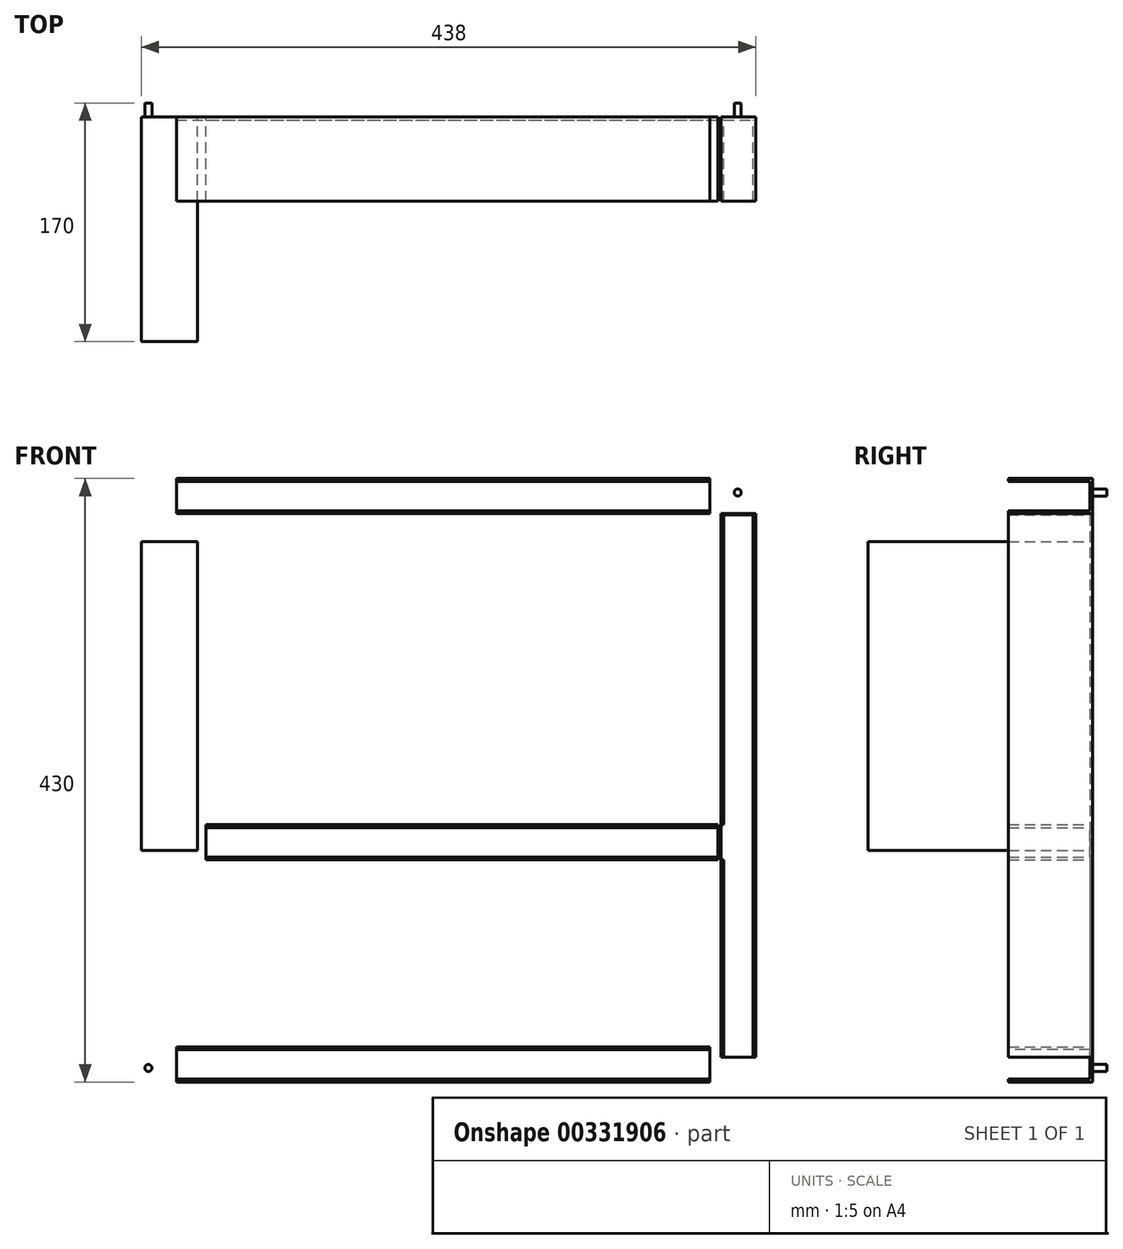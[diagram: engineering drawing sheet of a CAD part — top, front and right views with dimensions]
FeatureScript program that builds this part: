
annotation { "Feature Type Name" : "Feature", "Feature Type Description" : "" }
export const myFeature = defineFeature(function(context is Context, id is Id, definition is map)
    precondition{}
    {
        {
            var Q0;
            Q0=qCreatedBy(makeId("Front.planeOp"),FACE);
            var sketch = newSketch(context, id + "F0", { "sketchPlane" : qUnion([Q0])});
            skLineSegment(sketch, "E0.bottom", {"start": v(230, 225) * mm, "end": v(-230, 225) * mm});
            skLineSegment(sketch, "E0.top", {"start": v(230, -225) * mm, "end": v(-230, -225) * mm});
            skLineSegment(sketch, "E0.left", {"start": v(230, 225) * mm, "end": v(230, -225) * mm});
            skLineSegment(sketch, "E0.right", {"start": v(-230, 225) * mm, "end": v(-230, -225) * mm});
            skPoint(sketch, "E0.middle", {"position": v(0, 0) * mm});
            skSolve(sketch);
        }
        {
            var Q0;
            Q0=makeQuery(id+"F0.imprint","IMPRINT",FACE,{"disambiguationData":[TD([[makeQuery(id+"F0.imprint","IMPRINT",EDGE,{"derivedFrom":sQuery(id+"F0.wireOp",EDGE,"E0.bottom")}),1.0]])]});
            extrude(context, id + "F1", {"entities" : qUnion([Q0]), "depth" : 10 * mm});
        }
        {
            var Q0;
            Q0=makeQuery(id+"F1.opExtrude","CAP_FACE",FACE,{"disambiguationData":[OSD([sQuery(id+"F0.wireOp",EDGE,"E0.bottom"),sQuery(id+"F0.wireOp",EDGE,"E0.top"),sQuery(id+"F0.wireOp",EDGE,"E0.left"),sQuery(id+"F0.wireOp",EDGE,"E0.right")])],"isStart":false});
            var sketch = newSketch(context, id + "F2", { "sketchPlane" : qUnion([Q0])});
            skCircle(sketch, "E1", {"center": v(210, -205) * mm, "radius": 2.5 * mm});
            skCircle(sketch, "E2.MirrorC", {"center": v(-210, -205) * mm, "radius": 2.5 * mm});
            skCircle(sketch, "E3.MirrorC", {"center": v(-210, 205) * mm, "radius": 2.5 * mm});
            skCircle(sketch, "E4.MirrorC", {"center": v(210, 205) * mm, "radius": 2.5 * mm});
            skSolve(sketch);
        }
        {
            var Q0;
            Q0=makeQuery(id+"F2.imprint","IMPRINT",FACE,{"disambiguationData":[TD([[makeQuery(id+"F2.imprint","IMPRINT",EDGE,{"derivedFrom":sQuery(id+"F2.wireOp",EDGE,"E4.MirrorC")}),-1.0]])]});
            var Q1;
            Q1=makeQuery(id+"F2.imprint","IMPRINT",FACE,{"disambiguationData":[TD([[makeQuery(id+"F2.imprint","IMPRINT",EDGE,{"derivedFrom":sQuery(id+"F2.wireOp",EDGE,"E3.MirrorC")}),1.0]])]});
            var Q2;
            Q2=makeQuery(id+"F2.imprint","IMPRINT",FACE,{"disambiguationData":[TD([[makeQuery(id+"F2.imprint","IMPRINT",EDGE,{"derivedFrom":sQuery(id+"F2.wireOp",EDGE,"E2.MirrorC")}),-1.0]])]});
            var Q3;
            Q3=makeQuery(id+"F2.imprint","IMPRINT",FACE,{"disambiguationData":[TD([[makeQuery(id+"F2.imprint","IMPRINT",EDGE,{"derivedFrom":sQuery(id+"F2.wireOp",EDGE,"E1")}),1.0]])]});
            var Q4;
            Q4=sQuery(id+"F2.wireOp",EDGE,"E3.MirrorC");
            var Q5;
            Q5=sQuery(id+"F2.wireOp",EDGE,"E4.MirrorC");
            var Q6;
            Q6=sQuery(id+"F2.wireOp",EDGE,"E1");
            var Q7;
            Q7=sQuery(id+"F2.wireOp",EDGE,"E2.MirrorC");
            extrude(context, id + "F3", {"entities" : qUnion([Q0, Q1, Q2, Q3]), "operationType" : NewBodyOperationType.REMOVE, "surfaceEntities" : qUnion([Q4, Q5, Q6, Q7]), "oppositeDirection" : true, "depth" : 23 * mm});
        }
        {
            var Q0;
            Q0=makeQuery(id+"F1.opExtrude","CAP_FACE",FACE,{"disambiguationData":[OSD([sQuery(id+"F0.wireOp",EDGE,"E0.bottom"),sQuery(id+"F0.wireOp",EDGE,"E0.top"),sQuery(id+"F0.wireOp",EDGE,"E0.left"),sQuery(id+"F0.wireOp",EDGE,"E0.right")])],"isStart":false});
            var sketch = newSketch(context, id + "F4", { "sketchPlane" : qUnion([Q0])});
            skLineSegment(sketch, "E5.bottom", {"start": v(-215, 170) * mm, "end": v(-175, 170) * mm});
            skLineSegment(sketch, "E5.top", {"start": v(-215, -50) * mm, "end": v(-175, -50) * mm});
            skLineSegment(sketch, "E5.left", {"start": v(-215, 170) * mm, "end": v(-215, -50) * mm});
            skLineSegment(sketch, "E5.right", {"start": v(-175, 170) * mm, "end": v(-175, -50) * mm});
            skSolve(sketch);
        }
        {
            var Q0;
            Q0=makeQuery(id+"F4.imprint","IMPRINT",FACE,{"disambiguationData":[TD([[makeQuery(id+"F4.imprint","IMPRINT",EDGE,{"derivedFrom":sQuery(id+"F4.wireOp",EDGE,"E5.bottom")}),-1.0]])]});
            extrude(context, id + "F5", {"entities" : qUnion([Q0]), "operationType" : NewBodyOperationType.ADD, "depth" : 160 * mm});
        }
        {
            var Q0;
            Q0=makeQuery(id+"F1.opExtrude","CAP_FACE",FACE,{"disambiguationData":[OSD([sQuery(id+"F0.wireOp",EDGE,"E0.bottom"),sQuery(id+"F0.wireOp",EDGE,"E0.top"),sQuery(id+"F0.wireOp",EDGE,"E0.left"),sQuery(id+"F0.wireOp",EDGE,"E0.right")])],"isStart":false});
            var sketch = newSketch(context, id + "F6", { "sketchPlane" : qUnion([Q0])});
            skLineSegment(sketch, "E6.bottom", {"start": v(-190, 215) * mm, "end": v(190, 215) * mm});
            skLineSegment(sketch, "E6.top", {"start": v(-190, 190) * mm, "end": v(190, 190) * mm});
            skLineSegment(sketch, "E6.left", {"start": v(-190, 215) * mm, "end": v(-190, 190) * mm});
            skLineSegment(sketch, "E6.right", {"start": v(190, 215) * mm, "end": v(190, 190) * mm});
            skLineSegment(sketch, "E7.MirrorCS", {"start": v(190, -215) * mm, "end": v(190, -190) * mm});
            skLineSegment(sketch, "E8.MirrorCS", {"start": v(-190, -215) * mm, "end": v(-190, -190) * mm});
            skLineSegment(sketch, "E9.MirrorCS", {"start": v(-190, -215) * mm, "end": v(190, -215) * mm});
            skLineSegment(sketch, "E10.MirrorCS", {"start": v(-190, -190) * mm, "end": v(190, -190) * mm});
            skSolve(sketch);
        }
        {
            var Q0;
            Q0=makeQuery(id+"F6.imprint","IMPRINT",FACE,{"disambiguationData":[TD([[makeQuery(id+"F6.imprint","IMPRINT",EDGE,{"derivedFrom":sQuery(id+"F6.wireOp",EDGE,"E6.bottom")}),-1.0]])]});
            var Q1;
            Q1=makeQuery(id+"F6.imprint","IMPRINT",FACE,{"disambiguationData":[TD([[makeQuery(id+"F6.imprint","IMPRINT",EDGE,{"derivedFrom":sQuery(id+"F6.wireOp",EDGE,"E7.MirrorCS")}),1.0]])]});
            extrude(context, id + "F7", {"entities" : qUnion([Q0, Q1]), "operationType" : NewBodyOperationType.ADD, "depth" : 60 * mm});
        }
        {
            var Q0;
            Q0=makeQuery(id+"F7.opExtrude","SWEPT_FACE",FACE,{"disambiguationData":[OSD([sQuery(id+"F6.wireOp",EDGE,"E6.right")])]});
            var sketch = newSketch(context, id + "F8", { "sketchPlane" : qUnion([Q0])});
            skLineSegment(sketch, "E11.bottom", {"start": v(-70, 192) * mm, "end": v(-12, 192) * mm});
            skLineSegment(sketch, "E11.top", {"start": v(-70, 213) * mm, "end": v(-12, 213) * mm});
            skLineSegment(sketch, "E11.left", {"start": v(-70, 192) * mm, "end": v(-70, 213) * mm});
            skLineSegment(sketch, "E11.right", {"start": v(-12, 192) * mm, "end": v(-12, 213) * mm});
            skLineSegment(sketch, "E12", {"start": v(0, 0) * mm, "end": v(-11.07, 0) * mm, "construction": true});
            skLineSegment(sketch, "E13.MirrorCS", {"start": v(-70, -192) * mm, "end": v(-12, -192) * mm});
            skLineSegment(sketch, "E14.MirrorCS", {"start": v(-70, -213) * mm, "end": v(-12, -213) * mm});
            skLineSegment(sketch, "E15.MirrorCS", {"start": v(-12, -192) * mm, "end": v(-12, -213) * mm});
            skLineSegment(sketch, "E16", {"start": v(-70, -213) * mm, "end": v(-70, -192) * mm});
            skSolve(sketch);
        }
        {
            var Q0;
            Q0=makeQuery(id+"F8.imprint","IMPRINT",FACE,{"disambiguationData":[TD([[makeQuery(id+"F8.imprint","IMPRINT",EDGE,{"derivedFrom":sQuery(id+"F8.wireOp",EDGE,"E11.bottom")}),1.0]])]});
            extrude(context, id + "F9", {"entities" : qUnion([Q0]), "operationType" : NewBodyOperationType.REMOVE, "oppositeDirection" : true, "depth" : 382.2 * mm});
        }
        {
            var Q0;
            Q0=makeQuery(id+"F8.imprint","IMPRINT",FACE,{"disambiguationData":[TD([[makeQuery(id+"F8.imprint","IMPRINT",EDGE,{"derivedFrom":sQuery(id+"F8.wireOp",EDGE,"E13.MirrorCS")}),-1.0]])]});
            extrude(context, id + "F10", {"entities" : qUnion([Q0]), "operationType" : NewBodyOperationType.REMOVE, "oppositeDirection" : true, "depth" : 401 * mm});
        }
        {
            var Q0;
            Q0=makeQuery(id+"F1.opExtrude","CAP_FACE",FACE,{"disambiguationData":[OSD([sQuery(id+"F0.wireOp",EDGE,"E0.bottom"),sQuery(id+"F0.wireOp",EDGE,"E0.top"),sQuery(id+"F0.wireOp",EDGE,"E0.left"),sQuery(id+"F0.wireOp",EDGE,"E0.right")])],"isStart":false});
            var sketch = newSketch(context, id + "F11", { "sketchPlane" : qUnion([Q0])});
            skLineSegment(sketch, "E17.bottom", {"start": v(198, 190) * mm, "end": v(223, 190) * mm});
            skLineSegment(sketch, "E17.top", {"start": v(198, -197.5) * mm, "end": v(223, -197.5) * mm});
            skLineSegment(sketch, "E17.left", {"start": v(198, 190) * mm, "end": v(198, -197.5) * mm});
            skLineSegment(sketch, "E17.right", {"start": v(223, 190) * mm, "end": v(223, -197.5) * mm});
            skSolve(sketch);
        }
        {
            var Q0;
            Q0=makeQuery(id+"F11.imprint","IMPRINT",FACE,{"disambiguationData":[TD([[makeQuery(id+"F11.imprint","IMPRINT",EDGE,{"derivedFrom":sQuery(id+"F11.wireOp",EDGE,"E17.bottom")}),-1.0]])]});
            extrude(context, id + "F12", {"entities" : qUnion([Q0]), "operationType" : NewBodyOperationType.ADD, "depth" : 60 * mm});
        }
        {
            var Q0;
            Q0=makeQuery(id+"F12.opExtrude","SWEPT_FACE",FACE,{"disambiguationData":[OSD([sQuery(id+"F11.wireOp",EDGE,"E17.top")])]});
            var sketch = newSketch(context, id + "F13", { "sketchPlane" : qUnion([Q0])});
            skLineSegment(sketch, "E18.bottom", {"start": v(200, 70) * mm, "end": v(221, 70) * mm});
            skLineSegment(sketch, "E18.top", {"start": v(200, 12) * mm, "end": v(221, 12) * mm});
            skLineSegment(sketch, "E18.left", {"start": v(200, 70) * mm, "end": v(200, 12) * mm});
            skLineSegment(sketch, "E18.right", {"start": v(221, 70) * mm, "end": v(221, 12) * mm});
            skSolve(sketch);
        }
        {
            var Q0;
            Q0=makeQuery(id+"F13.imprint","IMPRINT",FACE,{"disambiguationData":[TD([[makeQuery(id+"F13.imprint","IMPRINT",EDGE,{"derivedFrom":sQuery(id+"F13.wireOp",EDGE,"E18.bottom")}),-1.0]])]});
            extrude(context, id + "F14", {"entities" : qUnion([Q0]), "operationType" : NewBodyOperationType.REMOVE, "oppositeDirection" : true, "depth" : 386.4 * mm});
        }
        {
            var Q0;
            Q0=makeQuery(id+"F12.opExtrude","SWEPT_FACE",FACE,{"disambiguationData":[OSD([sQuery(id+"F11.wireOp",EDGE,"E17.left")])]});
            var sketch = newSketch(context, id + "F15", { "sketchPlane" : qUnion([Q0])});
            skLineSegment(sketch, "E19.bottom", {"start": v(70, -31.72) * mm, "end": v(12, -31.72) * mm});
            skLineSegment(sketch, "E19.top", {"start": v(70, -56.72) * mm, "end": v(12, -56.72) * mm});
            skLineSegment(sketch, "E19.left", {"start": v(70, -31.72) * mm, "end": v(70, -56.72) * mm});
            skLineSegment(sketch, "E19.right", {"start": v(12, -31.72) * mm, "end": v(12, -56.72) * mm});
            skSolve(sketch);
        }
        {
            var Q0;
            Q0 = qSketchRegion(id + "F15", true);
            extrude(context, id + "F16", {"entities" : qUnion([Q0]), "operationType" : NewBodyOperationType.REMOVE, "oppositeDirection" : true, "depth" : 3.3 * mm});
        }
        {
            var Q0;
            Q0=makeQuery(id+"F1.opExtrude","CAP_FACE",FACE,{"disambiguationData":[OSD([sQuery(id+"F0.wireOp",EDGE,"E0.bottom"),sQuery(id+"F0.wireOp",EDGE,"E0.top"),sQuery(id+"F0.wireOp",EDGE,"E0.left"),sQuery(id+"F0.wireOp",EDGE,"E0.right")])],"isStart":false});
            var sketch = newSketch(context, id + "F17", { "sketchPlane" : qUnion([Q0])});
            skLineSegment(sketch, "E20.bottom", {"start": v(196, -31.72) * mm, "end": v(-169, -31.72) * mm});
            skLineSegment(sketch, "E20.top", {"start": v(196, -56.72) * mm, "end": v(-169, -56.72) * mm});
            skLineSegment(sketch, "E20.left", {"start": v(196, -31.72) * mm, "end": v(196, -56.72) * mm});
            skLineSegment(sketch, "E20.right", {"start": v(-169, -31.72) * mm, "end": v(-169, -56.72) * mm});
            skSolve(sketch);
        }
        {
            var Q0;
            Q0=makeQuery(id+"F17.imprint","IMPRINT",FACE,{"disambiguationData":[TD([[makeQuery(id+"F17.imprint","IMPRINT",EDGE,{"derivedFrom":sQuery(id+"F17.wireOp",EDGE,"E20.bottom")}),1.0]])]});
            extrude(context, id + "F18", {"entities" : qUnion([Q0]), "operationType" : NewBodyOperationType.ADD, "depth" : 60 * mm});
        }
        {
            var Q0;
            Q0=makeQuery(id+"F18.opExtrude","SWEPT_FACE",FACE,{"disambiguationData":[OSD([sQuery(id+"F17.wireOp",EDGE,"E20.left")])]});
            var sketch = newSketch(context, id + "F19", { "sketchPlane" : qUnion([Q0])});
            skLineSegment(sketch, "E21.bottom", {"start": v(-70, -54.72) * mm, "end": v(-12, -54.72) * mm});
            skLineSegment(sketch, "E21.top", {"start": v(-70, -33.72) * mm, "end": v(-12, -33.72) * mm});
            skLineSegment(sketch, "E21.left", {"start": v(-70, -54.72) * mm, "end": v(-70, -33.72) * mm});
            skLineSegment(sketch, "E21.right", {"start": v(-12, -54.72) * mm, "end": v(-12, -33.72) * mm});
            skSolve(sketch);
        }
        {
            var Q0;
            Q0=makeQuery(id+"F19.imprint","IMPRINT",FACE,{"disambiguationData":[TD([[makeQuery(id+"F19.imprint","IMPRINT",EDGE,{"derivedFrom":sQuery(id+"F19.wireOp",EDGE,"E21.bottom")}),1.0]])]});
            extrude(context, id + "F20", {"entities" : qUnion([Q0]), "operationType" : NewBodyOperationType.REMOVE, "oppositeDirection" : true, "depth" : 366.6 * mm});
        }
    });
